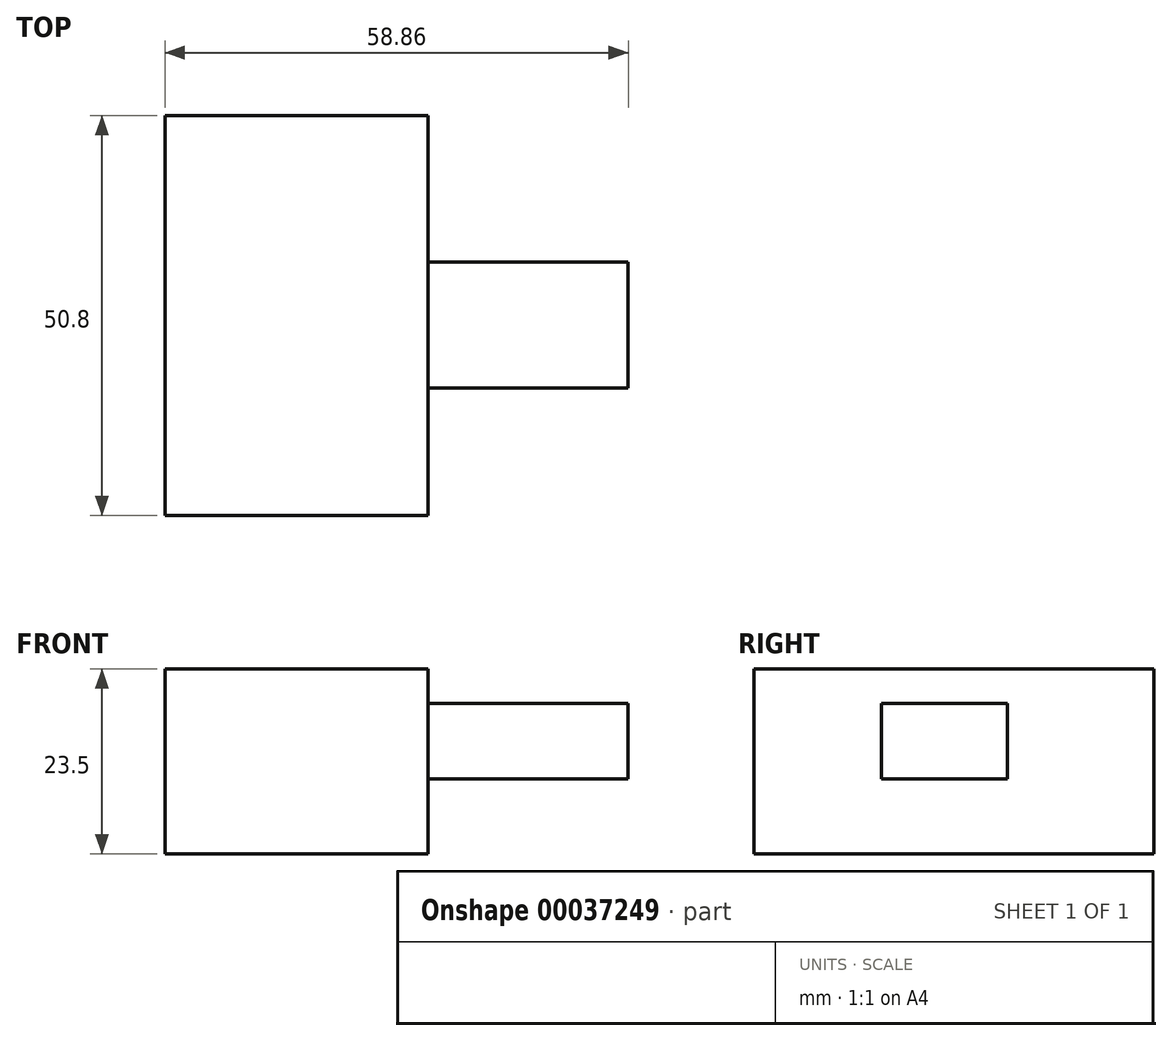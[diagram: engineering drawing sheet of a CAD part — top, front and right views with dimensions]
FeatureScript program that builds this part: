
annotation { "Feature Type Name" : "Feature", "Feature Type Description" : "" }
export const myFeature = defineFeature(function(context is Context, id is Id, definition is map)
    precondition{}
    {
        {
            var Q0;
            Q0=qCreatedBy(makeId("Front.planeOp"),FACE);
            var sketch = newSketch(context, id + "F0", { "sketchPlane" : qUnion([Q0])});
            skLineSegment(sketch, "E0.bottom", {"start": v(-75.08, 13.96) * mm, "end": v(-41.62, 13.96) * mm});
            skLineSegment(sketch, "E0.top", {"start": v(-75.08, -9.54) * mm, "end": v(-41.62, -9.54) * mm});
            skLineSegment(sketch, "E0.left", {"start": v(-75.08, 13.96) * mm, "end": v(-75.08, -9.54) * mm});
            skLineSegment(sketch, "E0.right", {"start": v(-41.62, 13.96) * mm, "end": v(-41.62, -9.54) * mm});
            skSolve(sketch);
        }
        {
            var Q0;
            Q0=makeQuery(id+"F0.imprint","IMPRINT",FACE,{"disambiguationData":[TD([[makeQuery(id+"F0.imprint","IMPRINT",EDGE,{"derivedFrom":sQuery(id+"F0.wireOp",EDGE,"E0.bottom")}),-1.0]])]});
            extrude(context, id + "F1", {"entities" : qUnion([Q0]), "depth" : 50.8 * mm});
        }
        {
            var Q0;
            Q0=makeQuery(id+"F1.opExtrude","SWEPT_FACE",FACE,{"disambiguationData":[OSD([sQuery(id+"F0.wireOp",EDGE,"E0.right")])]});
            var sketch = newSketch(context, id + "F2", { "sketchPlane" : qUnion([Q0])});
            skLineSegment(sketch, "E1.bottom", {"start": v(-34.62, 9.6) * mm, "end": v(-18.61, 9.6) * mm});
            skLineSegment(sketch, "E1.top", {"start": v(-34.62, 0) * mm, "end": v(-18.61, 0) * mm});
            skLineSegment(sketch, "E1.left", {"start": v(-34.62, 9.6) * mm, "end": v(-34.62, 0) * mm});
            skLineSegment(sketch, "E1.right", {"start": v(-18.61, 9.6) * mm, "end": v(-18.61, 0) * mm});
            skSolve(sketch);
        }
        {
            var Q0;
            Q0 = qSketchRegion(id + "F2", true);
            extrude(context, id + "F3", {"entities" : qUnion([Q0]), "operationType" : NewBodyOperationType.ADD, "depth" : 25.4 * mm});
        }
    });
